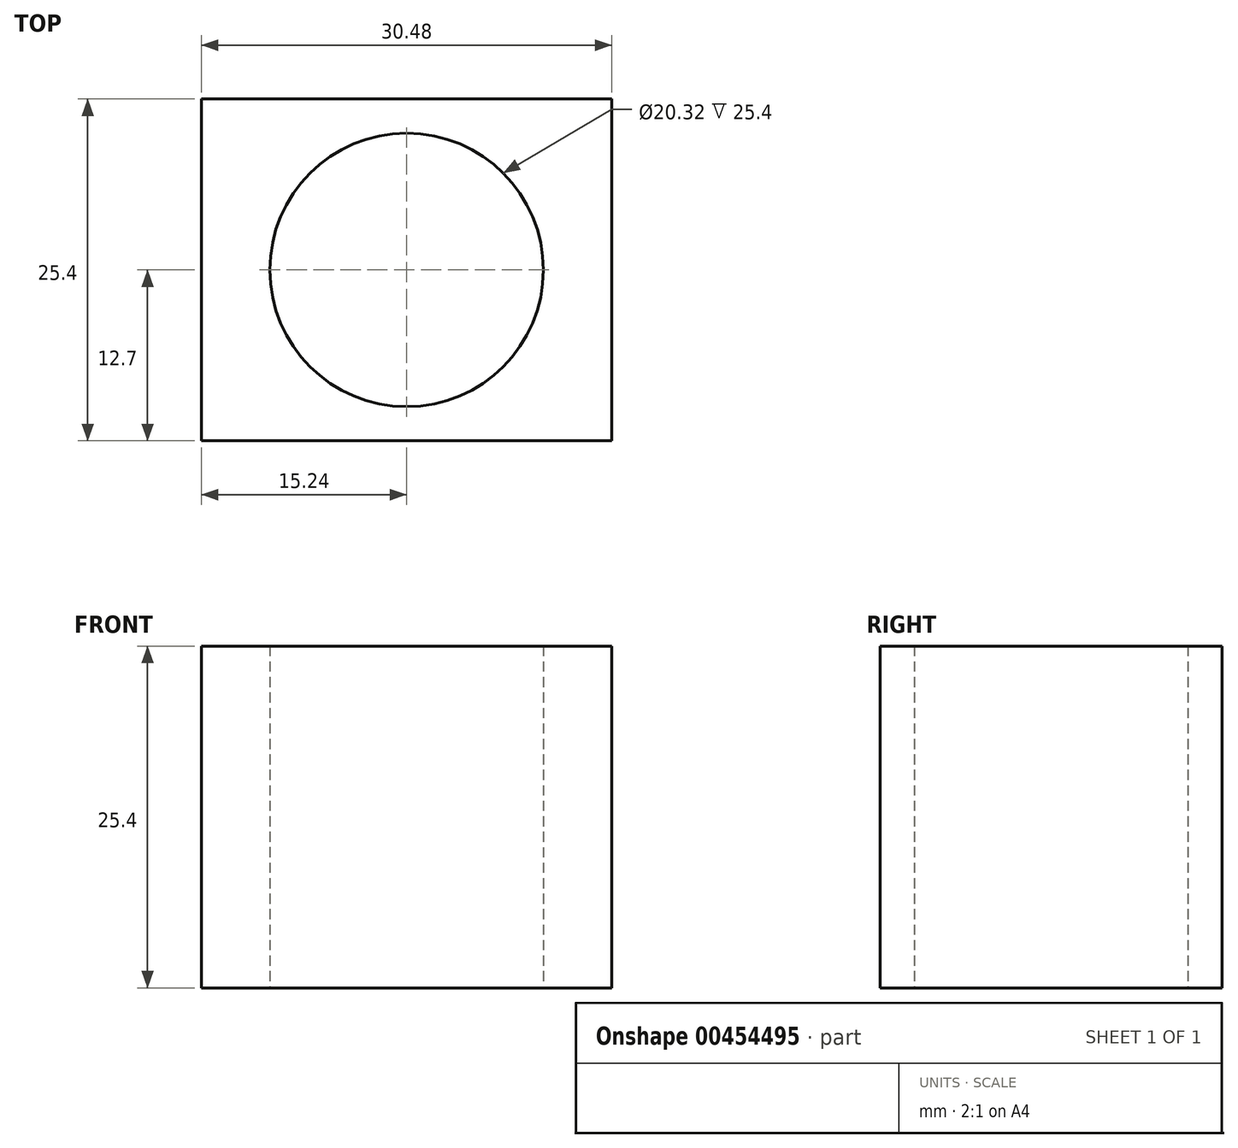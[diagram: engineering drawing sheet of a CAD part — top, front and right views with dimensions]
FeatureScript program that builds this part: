
annotation { "Feature Type Name" : "Feature", "Feature Type Description" : "" }
export const myFeature = defineFeature(function(context is Context, id is Id, definition is map)
    precondition{}
    {
        {
            var Q0;
            Q0=qCreatedBy(makeId("Top.planeOp"),FACE);
            var sketch = newSketch(context, id + "F0", { "sketchPlane" : qUnion([Q0])});
            skCircle(sketch, "E0", {"center": v(0, 0) * mm, "radius": 10.16 * mm});
            skLineSegment(sketch, "E1.bottom", {"start": v(-15.24, 12.7) * mm, "end": v(15.24, 12.7) * mm});
            skLineSegment(sketch, "E1.top", {"start": v(-15.24, -12.7) * mm, "end": v(15.24, -12.7) * mm});
            skLineSegment(sketch, "E1.left", {"start": v(-15.24, 12.7) * mm, "end": v(-15.24, -12.7) * mm});
            skLineSegment(sketch, "E1.right", {"start": v(15.24, 12.7) * mm, "end": v(15.24, -12.7) * mm});
            skSolve(sketch);
        }
        {
            var Q0;
            Q0 = qSketchRegion(id + "F0", true);
            extrude(context, id + "F1", {"entities" : qUnion([Q0]), "depth" : 25.4 * mm});
        }
    });
